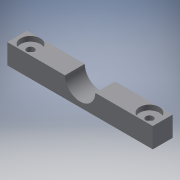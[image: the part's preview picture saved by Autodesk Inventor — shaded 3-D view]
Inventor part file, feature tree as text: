
AUTODESK INVENTOR PART (.ipt)
format: ipt  version: 2019.3 (Build 233278000, 278)  size: 117,760 bytes
history: native  units: in
note: dims shown in document units (in); Inventor stores cm internally (conversion verified against a paired STEP export)
features: sketch x3, extrude x2, hole x1
ambient origin geometry x8: Origin, YZ Plane, XZ Plane, XY Plane, X Axis, Y Axis, Z Axis, Center Point
bodies: Solid1 (feature_tree)
feature tree (6):
  extrude  "Extrusion1"  Depth=0.75in
  extrude  "Extrusion2"  Depth=0.7625in
  hole  "Hole1"  [1 undecoded]
  sketch  "Sketch1"  dims[d0=5.5in d1=0.75in]
  sketch  "Sketch2"  dims[d2=0.7625in d3=0.0in d4=1.15in]
  sketch  "Sketch3"  dims[d5=1.0in d6=0.0in d7=0.375in d8=0.5in d13=0.375in d14=0.5in d15=0.281in d16=0.75in d17=0.75in d18=0.188in d19=0.5635in d20=1.0in d21=0.0in]
note: 1 required parameter value undecoded (feature->parameter linkage not recoverable at this tier; creation-order binding heuristic only, values carry confidence <= 0.55)
